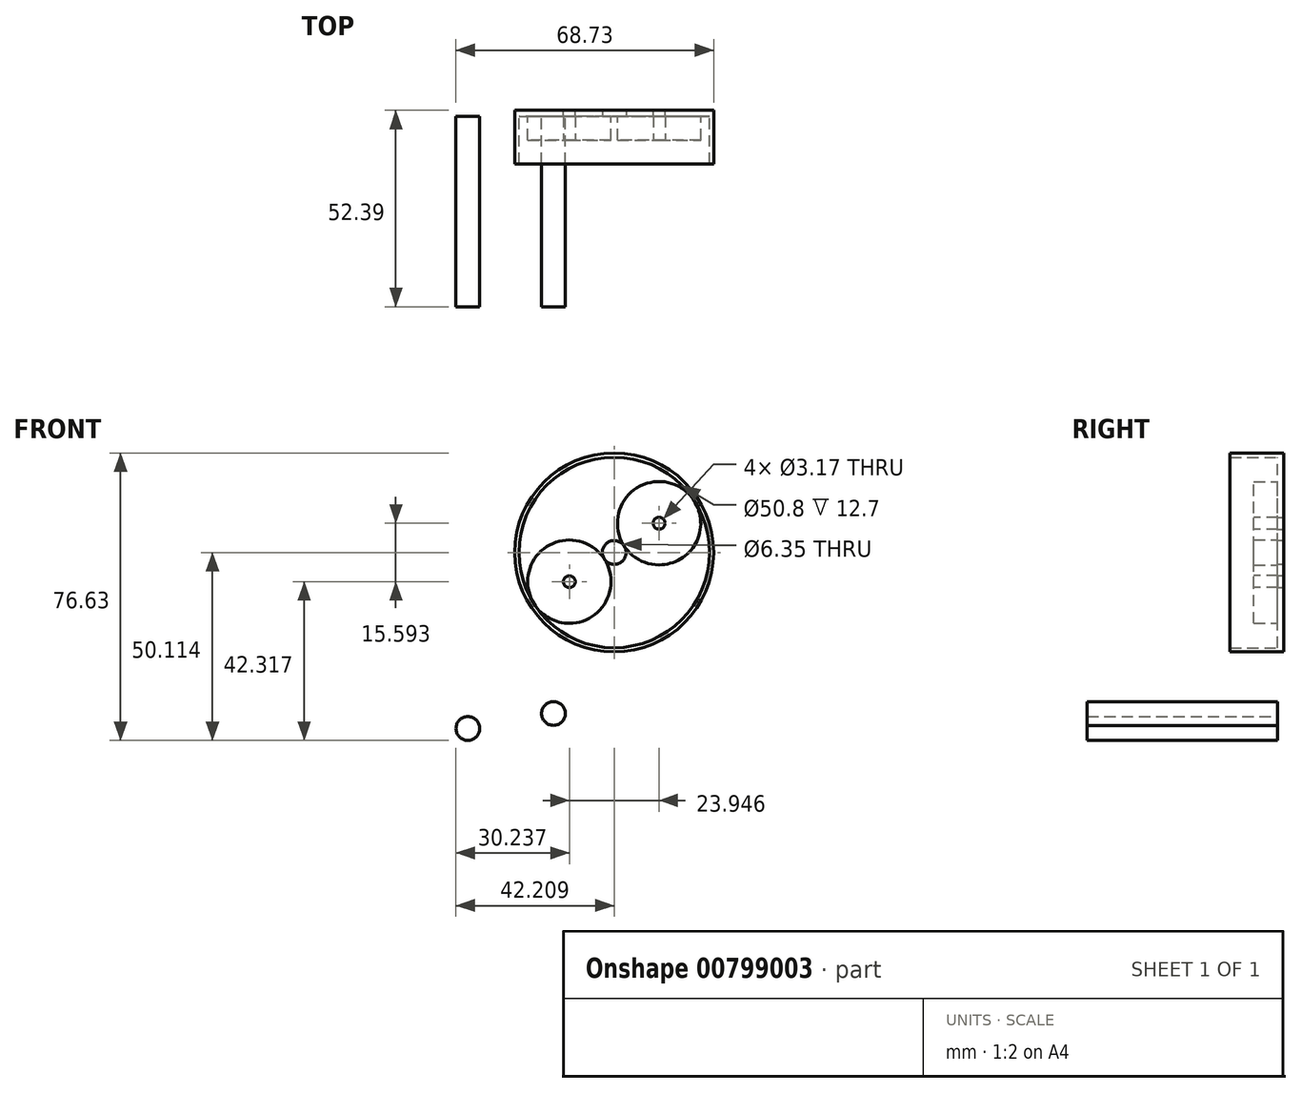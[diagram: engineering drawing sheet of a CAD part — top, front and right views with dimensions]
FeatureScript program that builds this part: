
annotation { "Feature Type Name" : "Feature", "Feature Type Description" : "" }
export const myFeature = defineFeature(function(context is Context, id is Id, definition is map)
    precondition{}
    {
        {
            var Q0;
            Q0=qCreatedBy(makeId("Front.planeOp"),FACE);
            var sketch = newSketch(context, id + "F0", { "sketchPlane" : qUnion([Q0])});
            skCircle(sketch, "E0", {"center": v(0, 0) * mm, "radius": 3.18 * mm});
            skCircle(sketch, "E1", {"center": v(22.83, 4) * mm, "radius": 3.17 * mm});
            skSolve(sketch);
        }
        {
            var Q0;
            Q0=makeQuery(id+"F0.imprint","IMPRINT",FACE,{"disambiguationData":[TD([[makeQuery(id+"F0.imprint","IMPRINT",EDGE,{"derivedFrom":sQuery(id+"F0.wireOp",EDGE,"E0")}),1.0]])]});
            extrude(context, id + "F1", {"entities" : qUnion([Q0]), "depth" : 50.8 * mm, "offsetDistance" : 25.4 * mm});
        }
        {
            var Q0;
            Q0=makeQuery(id+"F0.imprint","IMPRINT",FACE,{"disambiguationData":[TD([[makeQuery(id+"F0.imprint","IMPRINT",EDGE,{"derivedFrom":sQuery(id+"F0.wireOp",EDGE,"E1")}),1.0]])]});
            extrude(context, id + "F2", {"entities" : qUnion([Q0]), "depth" : 50.8 * mm, "offsetDistance" : 25.4 * mm});
        }
        {
            var Q0;
            Q0=qCreatedBy(makeId("Front.planeOp"),FACE);
            var sketch = newSketch(context, id + "F3", { "sketchPlane" : qUnion([Q0])});
            skCircle(sketch, "E2", {"center": v(39.03, 46.93) * mm, "radius": 25.4 * mm});
            skCircle(sketch, "E3", {"center": v(39.03, 46.93) * mm, "radius": 3.18 * mm});
            skPoint(sketch, "E4", {"position": v(51, 54.73) * mm});
            skPoint(sketch, "E5", {"position": v(27.06, 39.14) * mm});
            skLineSegment(sketch, "E6", {"start": v(17.74, 33.07) * mm, "end": v(60.31, 60.8) * mm, "construction": true});
            skCircle(sketch, "E7", {"center": v(51, 54.73) * mm, "radius": 11.11 * mm});
            skCircle(sketch, "E8", {"center": v(27.06, 39.14) * mm, "radius": 11.11 * mm});
            skCircle(sketch, "E9", {"center": v(39.03, 46.93) * mm, "radius": 26.52 * mm});
            skSolve(sketch);
        }
        {
            var Q0;
            Q0=makeQuery(id+"F3.imprint","IMPRINT",FACE,{"disambiguationData":[TD([[makeQuery(id+"F3.imprint","IMPRINT",EDGE,{"derivedFrom":sQuery(id+"F3.wireOp",EDGE,"E9")}),1.0]])]});
            extrude(context, id + "F4", {"entities" : qUnion([Q0]), "operationType" : NewBodyOperationType.ADD, "depth" : 12.7 * mm, "offsetDistance" : 25.4 * mm});
        }
        {
            var Q0;
            Q0=makeQuery(id+"F3.imprint","IMPRINT",FACE,{"disambiguationData":[TD([[makeQuery(id+"F3.imprint","IMPRINT",EDGE,{"derivedFrom":sQuery(id+"F3.wireOp",EDGE,"E9")}),1.0]])]});
            extrude(context, id + "F5", {"entities" : qUnion([Q0]), "operationType" : NewBodyOperationType.ADD, "oppositeDirection" : true, "depth" : 1.59 * mm, "offsetDistance" : 25.4 * mm});
        }
        {
            var Q0;
            {var subQ0=sQuery(id+"F3.wireOp",EDGE,"E8");var subQ1=makeQuery(id+"F3.imprint","INTERSECT",VERTEX,{"derivedFrom":[sQuery(id+"F3.wireOp",EDGE,"E2"),subQ0]});Q0=makeQuery(id+"F3.imprint","IMPRINT",FACE,{"disambiguationData":[TD([[makeQuery(id+"F3.imprint","IMPRINT",EDGE,{"disambiguationData":[TD([[subQ1,1.0]])],"derivedFrom":subQ0}),1.0]])]});}
            var Q1;
            {var subQ0=sQuery(id+"F3.wireOp",EDGE,"E7");var subQ1=makeQuery(id+"F3.imprint","INTERSECT",VERTEX,{"derivedFrom":[sQuery(id+"F3.wireOp",EDGE,"E2"),subQ0]});Q1=makeQuery(id+"F3.imprint","IMPRINT",FACE,{"disambiguationData":[TD([[makeQuery(id+"F3.imprint","IMPRINT",EDGE,{"disambiguationData":[TD([[subQ1,-1.0]])],"derivedFrom":subQ0}),1.0]])]});}
            var Q2;
            {var subQ0=sQuery(id+"F3.wireOp",EDGE,"E7");var subQ1=sQuery(id+"F3.wireOp",EDGE,"E2");var subQ2=makeQuery(id+"F3.imprint","INTERSECT",VERTEX,{"derivedFrom":[subQ1,subQ0]});Q2=makeQuery(id+"F3.imprint","IMPRINT",FACE,{"disambiguationData":[TD([[makeQuery(id+"F3.imprint","IMPRINT",EDGE,{"disambiguationData":[TD([[subQ2,1.0]])],"derivedFrom":subQ1}),1.0]])]});}
            var Q3;
            {var subQ0=sQuery(id+"F3.wireOp",EDGE,"E7");var subQ1=sQuery(id+"F3.wireOp",EDGE,"E2");var subQ2=makeQuery(id+"F3.imprint","INTERSECT",VERTEX,{"derivedFrom":[subQ1,subQ0]});Q3=makeQuery(id+"F3.imprint","IMPRINT",FACE,{"disambiguationData":[TD([[makeQuery(id+"F3.imprint","IMPRINT",EDGE,{"disambiguationData":[TD([[subQ2,-1.0]])],"derivedFrom":subQ1}),1.0]])]});}
            extrude(context, id + "F6", {"entities" : qUnion([Q0, Q1, Q2, Q3]), "operationType" : NewBodyOperationType.ADD, "oppositeDirection" : true, "depth" : 1.59 * mm, "offsetDistance" : 25.4 * mm});
        }
        {
            var Q0;
            {var subQ0=sQuery(id+"F3.wireOp",EDGE,"E7");var subQ1=makeQuery(id+"F3.imprint","INTERSECT",VERTEX,{"derivedFrom":[sQuery(id+"F3.wireOp",EDGE,"E2"),subQ0]});Q0=makeQuery(id+"F3.imprint","IMPRINT",FACE,{"disambiguationData":[TD([[makeQuery(id+"F3.imprint","IMPRINT",EDGE,{"disambiguationData":[TD([[subQ1,-1.0]])],"derivedFrom":subQ0}),1.0]])]});}
            var Q1;
            {var subQ0=sQuery(id+"F3.wireOp",EDGE,"E8");var subQ1=makeQuery(id+"F3.imprint","INTERSECT",VERTEX,{"derivedFrom":[sQuery(id+"F3.wireOp",EDGE,"E2"),subQ0]});Q1=makeQuery(id+"F3.imprint","IMPRINT",FACE,{"disambiguationData":[TD([[makeQuery(id+"F3.imprint","IMPRINT",EDGE,{"disambiguationData":[TD([[subQ1,1.0]])],"derivedFrom":subQ0}),1.0]])]});}
            extrude(context, id + "F7", {"entities" : qUnion([Q0, Q1]), "depth" : 6.35 * mm, "offsetDistance" : 25.4 * mm});
        }
        {
            var Q0;
            Q0=sQuery(id+"F3.wireOp",VERTEX,"E5");
            var Q1;
            Q1=sQuery(id+"F3.wireOp",VERTEX,"E4");
            var Q2;
            Q2=makeQuery(id+"F7.opExtrude","SWEPT_BODY",BODY,{"disambiguationData":[OSD([sQuery(id+"F3.wireOp",EDGE,"E8")])]});
            var Q3;
            Q3=makeQuery(id+"F7.opExtrude","SWEPT_BODY",BODY,{"disambiguationData":[OSD([sQuery(id+"F3.wireOp",EDGE,"E7")])]});
            hole(context, id + "F8", {"style" : HoleStyle.SIMPLE, "endStyle" : HoleEndStyle.THROUGH, "oppositeDirection" : true, "holeDiameter" : 3.17 * mm, "majorDiameter" : 6.35 * mm, "isTappedThrough" : true, "tappedDepth" : 12.7 * mm, "tapClearance" : 3, "locations" : qUnion([Q0, Q1]), "scope" : qUnion([Q2, Q3]), "startStyle" : HoleStartStyle.PART});
        }
        {
            var Q0;
            Q0=sQuery(id+"F3.wireOp",VERTEX,"E4");
            var Q1;
            Q1=sQuery(id+"F3.wireOp",VERTEX,"E5");
            var Q2;
            Q2=makeQuery(id+"F4.opExtrude","SWEPT_BODY",BODY,{"disambiguationData":[OSD([sQuery(id+"F3.wireOp",EDGE,"E2"),sQuery(id+"F3.wireOp",EDGE,"E9")])]});
            hole(context, id + "F9", {"style" : HoleStyle.SIMPLE, "endStyle" : HoleEndStyle.THROUGH, "holeDiameter" : 3.17 * mm, "majorDiameter" : 6.35 * mm, "isTappedThrough" : true, "tappedDepth" : 12.7 * mm, "tapClearance" : 3, "locations" : qUnion([Q0, Q1]), "scope" : qUnion([Q2]), "startStyle" : HoleStartStyle.PART});
        }
    });
